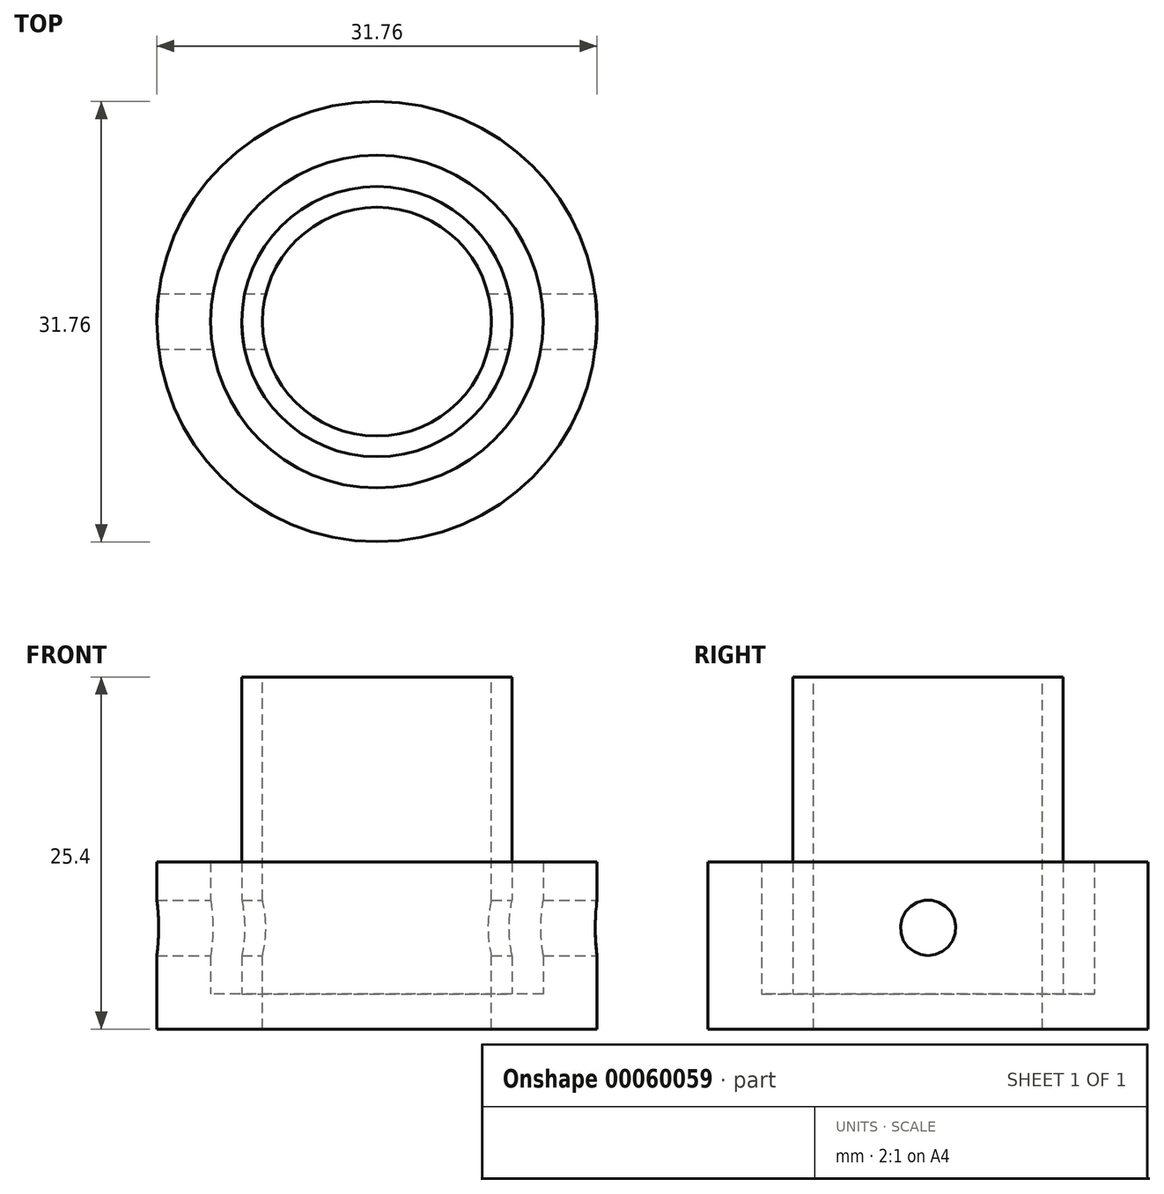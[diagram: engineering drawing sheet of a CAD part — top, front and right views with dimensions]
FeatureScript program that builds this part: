
annotation { "Feature Type Name" : "Feature", "Feature Type Description" : "" }
export const myFeature = defineFeature(function(context is Context, id is Id, definition is map)
    precondition{}
    {
        {
            var Q0;
            Q0=qCreatedBy(makeId("Top.planeOp"),FACE);
            var sketch = newSketch(context, id + "F0", { "sketchPlane" : qUnion([Q0])});
            skCircle(sketch, "E0", {"center": v(0, 0) * mm, "radius": 9.75 * mm});
            skSolve(sketch);
        }
        {
            var Q0;
            Q0 = qSketchRegion(id + "F0", true);
            extrude(context, id + "F1", {"entities" : qUnion([Q0]), "depth" : 25.4 * mm});
        }
        {
            var Q0;
            Q0=makeQuery(id+"F1.opExtrude","CAP_FACE",FACE,{"disambiguationData":[OSD([sQuery(id+"F0.wireOp",EDGE,"E0")])],"isStart":false});
            var sketch = newSketch(context, id + "F2", { "sketchPlane" : qUnion([Q0])});
            skCircle(sketch, "E1", {"center": v(0, 0) * mm, "radius": 8.26 * mm});
            skSolve(sketch);
        }
        {
            var Q0;
            Q0 = qSketchRegion(id + "F2", true);
            extrude(context, id + "F3", {"entities" : qUnion([Q0]), "operationType" : NewBodyOperationType.REMOVE, "oppositeDirection" : true, "depth" : 25.4 * mm});
        }
        {
            var Q0;
            Q0=makeQuery(id+"F1.opExtrude","CAP_FACE",FACE,{"disambiguationData":[OSD([sQuery(id+"F0.wireOp",EDGE,"E0")])],"isStart":true});
            var sketch = newSketch(context, id + "F4", { "sketchPlane" : qUnion([Q0])});
            skCircle(sketch, "E2", {"center": v(0, 0) * mm, "radius": 8.26 * mm});
            skCircle(sketch, "E3", {"center": v(0, 0) * mm, "radius": 15.88 * mm});
            skSolve(sketch);
        }
        {
            var Q0;
            Q0=makeQuery(id+"F4.imprint","IMPRINT",FACE,{"disambiguationData":[TD([[makeQuery(id+"F4.imprint","IMPRINT",EDGE,{"derivedFrom":sQuery(id+"F4.wireOp",EDGE,"E3")}),1.0]])]});
            var Q1;
            Q1=makeQuery(id+"F4.imprint","IMPRINT",FACE,{"disambiguationData":[TD([[makeQuery(id+"F4.imprint","IMPRINT",EDGE,{"derivedFrom":sQuery(id+"F4.wireOp",EDGE,"E2")}),1.0]])]});
            extrude(context, id + "F5", {"entities" : qUnion([Q0, Q1]), "operationType" : NewBodyOperationType.ADD, "oppositeDirection" : true, "depth" : 2.54 * mm});
        }
        {
            var Q0;
            Q0=makeQuery(id+"F5.opExtrude","CAP_FACE",FACE,{"disambiguationData":[OSD([sQuery(id+"F4.wireOp",EDGE,"E2"),sQuery(id+"F4.wireOp",EDGE,"E3")])],"isStart":false});
            var sketch = newSketch(context, id + "F6", { "sketchPlane" : qUnion([Q0])});
            skCircle(sketch, "E4", {"center": v(0, 0) * mm, "radius": 15.88 * mm});
            skCircle(sketch, "E5", {"center": v(0, 0) * mm, "radius": 12 * mm});
            skSolve(sketch);
        }
        {
            var Q0;
            Q0 = qSketchRegion(id + "F6", true);
            extrude(context, id + "F7", {"entities" : qUnion([Q0]), "operationType" : NewBodyOperationType.ADD, "depth" : 9.52 * mm});
        }
        {
            var Q0;
            Q0=qCreatedBy(makeId("Right.planeOp"),FACE);
            var sketch = newSketch(context, id + "F8", { "sketchPlane" : qUnion([Q0])});
            skLineSegment(sketch, "E6", {"start": v(0, 0) * mm, "end": v(0, 9.1) * mm});
            skCircle(sketch, "E7", {"center": v(0, 7.3) * mm, "radius": 2 * mm});
            skSolve(sketch);
        }
        {
            var Q0;
            Q0 = qSketchRegion(id + "F8", true);
            extrude(context, id + "F9", {"entities" : qUnion([Q0]), "operationType" : NewBodyOperationType.REMOVE, "oppositeDirection" : true, "depth" : 25.4 * mm, "hasSecondDirection" : true, "secondDirectionOppositeDirection" : false, "secondDirectionDepth" : 25.4 * mm});
        }
    });
